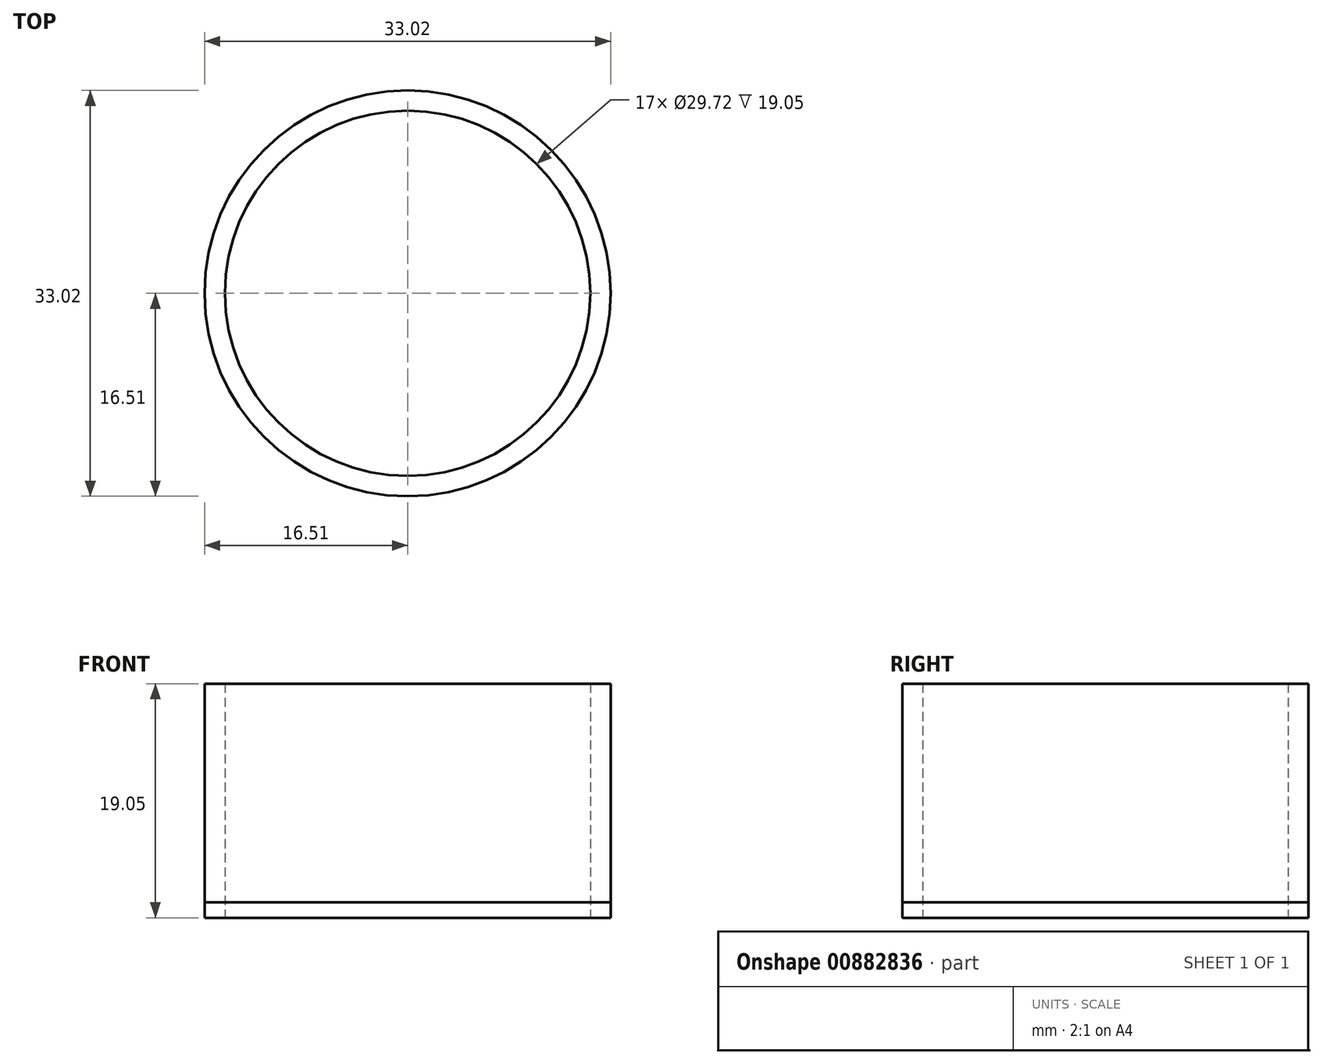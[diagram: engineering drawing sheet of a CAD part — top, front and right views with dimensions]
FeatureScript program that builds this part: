
annotation { "Feature Type Name" : "Feature", "Feature Type Description" : "" }
export const myFeature = defineFeature(function(context is Context, id is Id, definition is map)
    precondition{}
    {
        {
            var Q0;
            Q0=qCreatedBy(makeId("Top.planeOp"),FACE);
            var sketch = newSketch(context, id + "F0", { "sketchPlane" : qUnion([Q0])});
            skCircle(sketch, "E0", {"center": v(0, 0) * mm, "radius": 14.86 * mm});
            skCircle(sketch, "E1", {"center": v(0, 0) * mm, "radius": 1.65 * mm});
            skCircle(sketch, "E2", {"center": v(0, 0) * mm, "radius": 16.51 * mm});
            skCircle(sketch, "E3", {"center": v(0, 0) * mm, "radius": 2.92 * mm});
            skSolve(sketch);
        }
        {
            var Q0;
            Q0 = qSketchRegion(id + "F0", true);
            extrude(context, id + "F1", {"entities" : qUnion([Q0]), "depth" : 19.05 * mm, "offsetDistance" : 25.4 * mm});
        }
        {
            var Q0;
            Q0=qCreatedBy(makeId("Top.planeOp"),FACE);
            var sketch = newSketch(context, id + "F2", { "sketchPlane" : qUnion([Q0])});
            skCircle(sketch, "E4", {"center": v(0, 0) * mm, "radius": 16.51 * mm});
            skSolve(sketch);
        }
        {
            var Q0;
            Q0 = qSketchRegion(id + "F2", true);
            extrude(context, id + "F3", {"entities" : qUnion([Q0]), "depth" : 1.27 * mm, "offsetDistance" : 25.4 * mm});
        }
    });
